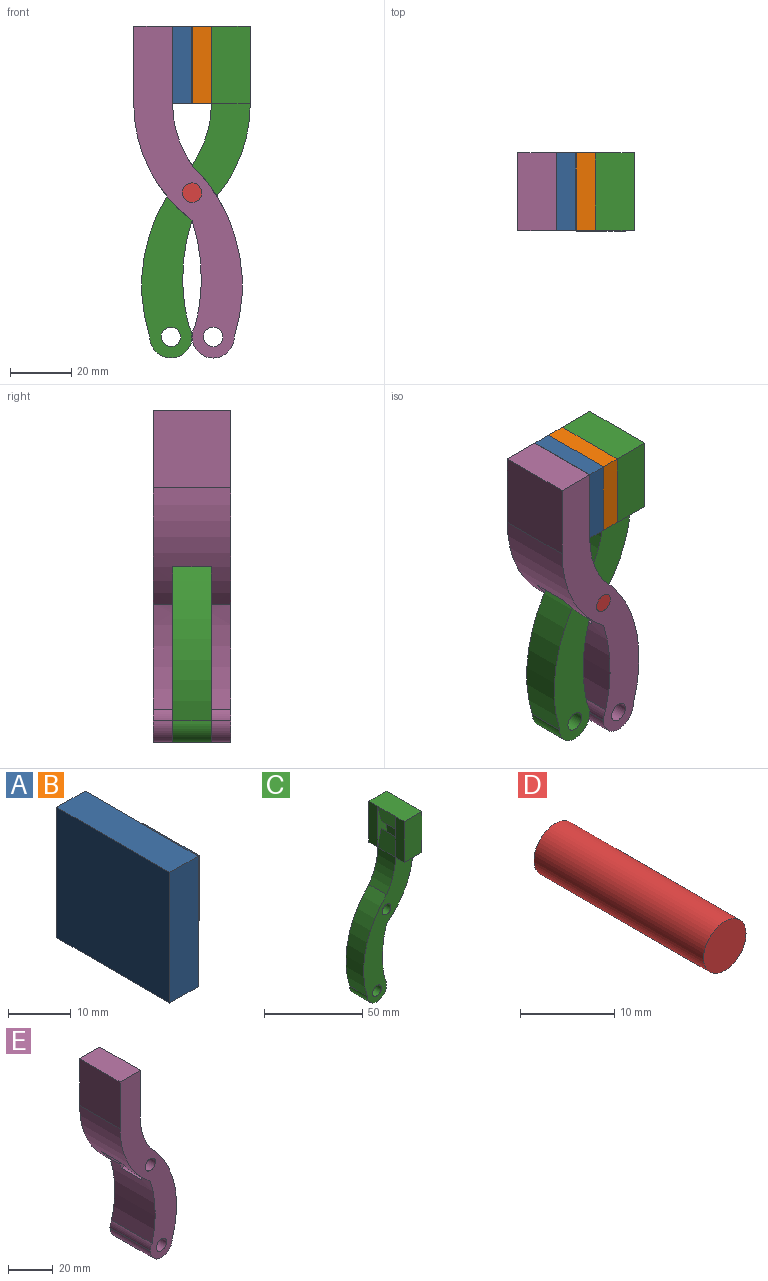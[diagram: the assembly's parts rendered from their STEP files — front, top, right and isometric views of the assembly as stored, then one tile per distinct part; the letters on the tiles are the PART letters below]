
ASSEMBLY  parts=5 mates=8
PART A: 14 faces, bbox 12.9x25.4x25.4 mm
  f0: plane 12.7x10.31mm, normal (0.97,0,-0.23), area 134.7mm2, adj f1,f5,f6,f8
  f1: plane 12.7x4.11mm, normal (-0.69,0,-0.72), area 72.5mm2, adj f0,f2,f5,f6
  f2: plane 12.7x12.7mm, normal (1,0,0), area 161.3mm2, adj f1,f3,f5,f6
  f3: plane 12.7x4.11mm, normal (-0.69,0,0.72), area 72.5mm2, adj f2,f4,f5,f6
  f4: plane 12.7x10.31mm, normal (0.97,0,0.23), area 134.7mm2, adj f3,f5,f6,f10
  f5: plane 25.4x6.59mm, normal (0,-1,0), area 73.3mm2, adj f0,f1,f2,f3,f4,f7
  f6: plane 25.4x6.59mm, normal (0,1,0), area 73.3mm2, adj f0,f1,f2,f3,f4,f9
  f7: plane 25.4x6.35mm, normal (1,0,0), area 161.3mm2, adj f5,f8,f10,f12
  f8: plane 25.4x6.35mm, normal (0,0,-1), area 161.3mm2, adj f0,f7,f9,f11,f12,f13
  f9: plane 25.4x6.35mm, normal (1,0,0), area 161.3mm2, adj f6,f8,f10,f13
  f10: plane 25.4x6.35mm, normal (0,0,1), area 161.3mm2, adj f4,f7,f9,f11,f12,f13
  f11: plane 25.4x25.4mm, normal (-1,0,0), area 645.2mm2, adj f8,f10,f12,f13
  f12: plane 25.4x6.35mm, normal (0,-1,0), area 161.3mm2, adj f7,f8,f10,f11
  f13: plane 25.4x6.35mm, normal (0,1,0), area 161.3mm2, adj f8,f9,f10,f11
PART B: same geometry as A
PART C: 24 faces, bbox 35.5x25.4x108.5 mm
  f0: plane 12.7x6.35mm, normal (0,0,-1), area 80.6mm2, adj f1,f5,f7,f22
  f1: plane 25.4x6.35mm, normal (-1,0,0), area 161.3mm2, adj f0,f2,f7,f13
  f2: plane 25.4x12.7mm, normal (0,0,1), area 322.6mm2, adj f1,f3,f5,f6,f7,f12
  f3: plane 25.4x6.35mm, normal (-1,0,0), area 161.3mm2, adj f2,f4,f6,f14
  f4: plane 12.7x6.35mm, normal (0,0,-1), area 80.6mm2, adj f3,f5,f6,f23
  f5: plane 25.4x25.4mm, normal (1,0,0), area 645.2mm2, adj f0,f2,f4,f6,f7,f20
  f6: plane 25.4x12.7mm, normal (0,1,0), area 322.6mm2, adj f2,f3,f4,f5
  f7: plane 25.4x12.7mm, normal (0,-1,0), area 322.6mm2, adj f0,f1,f2,f5
  f8: plane 12.7x10.31mm, normal (-0.97,0,0.23), area 134.7mm2, adj f9,f13,f14,f15
  f9: plane 12.7x4.11mm, normal (0.69,0,0.72), area 72.5mm2, adj f8,f10,f13,f14
  f10: plane 12.7x12.7mm, normal (-1,0,0), area 161.3mm2, adj f9,f11,f13,f14
  f11: plane 12.7x4.11mm, normal (0.69,0,-0.72), area 72.5mm2, adj f10,f12,f13,f14
  f12: plane 12.7x10.31mm, normal (-0.97,0,-0.23), area 134.7mm2, adj f2,f11,f13,f14
  f13: plane 25.4x6.59mm, normal (0,1,0), area 73.3mm2, adj f1,f8,f9,f10,f11,f12
  f14: plane 25.4x6.59mm, normal (0,-1,0), area 73.3mm2, adj f3,f8,f9,f10,f11,f12
  f15: cylinder r=34.92mm len=20.08mm, axis (0,1,0), area 271.7mm2, adj f8,f16,f22,f23
  f16: cylinder r=55.15mm len=56.19mm, axis (0,1,0), area 773.6mm2, adj f15,f17,f22,f23
  f17: cylinder r=6.91mm len=13.82mm, axis (0,1,0), area 325.1mm2, adj f16,f18,f22,f23
  f18: cylinder r=60.77mm len=34.41mm, axis (0,1,0), area 443.3mm2, adj f17,f20,f22,f23
  f19: cylinder r=3.17mm len=12.7mm, axis (0,1,0), area 253.4mm2, adj f22,f23
  f20: cylinder r=47.62mm len=38.1mm, axis (0,1,0), area 560.9mm2, adj f5,f18,f22,f23
  f21: cylinder r=3.17mm len=12.7mm, axis (0,1,0), area 253.4mm2, adj f22,f23
  f22: plane 83.14x35.52mm, normal (0,-1,0), area 1063.8mm2, adj f0,f15,f16,f17,f18,f19,f20,f21
  f23: plane 83.14x35.52mm, normal (0,1,0), area 1063.8mm2, adj f4,f15,f16,f17,f18,f19,f20,f21
PART D: 3 faces, bbox 6.4x25.4x6.4 mm
  f0: cylinder r=3.17mm len=25.4mm, axis (0,1,0), area 506.7mm2, adj f1,f2
  f1: plane 6.35x6.35mm, normal (0,-1,0), area 31.7mm2, adj f0
  f2: plane 6.35x6.35mm, normal (0,1,0), area 31.7mm2, adj f0
PART E: 27 faces, bbox 35.5x25.4x108.5 mm
  f0: cylinder r=3.17mm len=6.35mm, axis (0,1,0), area 126.7mm2, adj f9,f26
  f1: cylinder r=47.62mm len=38.1mm, axis (0,1,0), area 906.9mm2, adj f2,f8,f9,f10,f23,f25,f26
  f2: cylinder r=60.77mm len=34.41mm, axis (0,1,0), area 848.3mm2, adj f1,f9,f10,f18,f24,f25,f26
  f3: cylinder r=55.15mm len=56.19mm, axis (0,1,0), area 1318mm2, adj f4,f9,f10,f20,f24,f25,f26
  f4: cylinder r=34.92mm len=25.4mm, axis (0,1,0), area 501.4mm2, adj f3,f5,f6,f9,f10,f12,f23,f25
  f5: plane 25.4x6.35mm, normal (1,0,0), area 161.3mm2, adj f4,f7,f10,f16
  f6: plane 25.4x6.35mm, normal (1,0,0), area 161.3mm2, adj f4,f7,f9,f17
  f7: plane 25.4x12.7mm, normal (0,0,1), area 322.6mm2, adj f5,f6,f8,f9,f10,f13
  f8: plane 25.4x25.4mm, normal (-1,0,0), area 645.2mm2, adj f1,f7,f9,f10
  f9: plane 108.54x35.52mm, normal (0,1,0), area 1386.4mm2, adj f0,f1,f2,f3,f4,f6,f7,f8
  f10: plane 108.54x35.52mm, normal (0,-1,0), area 1386.4mm2, adj f1,f2,f3,f4,f5,f7,f8,f18
  f11: plane 12.7x4.11mm, normal (-0.69,0,0.72), area 72.5mm2, adj f12,f15,f16,f17
  f12: plane 12.7x10.31mm, normal (0.97,0,0.23), area 134.7mm2, adj f4,f11,f16,f17
  f13: plane 12.7x10.31mm, normal (0.97,0,-0.23), area 134.7mm2, adj f7,f14,f16,f17
  f14: plane 12.7x4.11mm, normal (-0.69,0,-0.72), area 72.5mm2, adj f13,f15,f16,f17
  f15: plane 12.7x12.7mm, normal (1,0,0), area 161.3mm2, adj f11,f14,f16,f17
  f16: plane 25.4x6.59mm, normal (0,1,0), area 73.3mm2, adj f5,f11,f12,f13,f14,f15
  f17: plane 25.4x6.59mm, normal (0,-1,0), area 73.3mm2, adj f6,f11,f12,f13,f14,f15
  f18: cylinder r=6.91mm len=25.4mm, axis (0,1,0), area 99mm2, adj f2,f9,f10,f19
  f19: cylinder r=6.91mm len=25.4mm, axis (0,1,0), area 1.8mm2, adj f9,f10,f18,f20
  f20: cylinder r=6.91mm len=25.4mm, axis (0,1,0), area 549.5mm2, adj f3,f9,f10,f19
  f21: cylinder r=3.17mm len=6.35mm, axis (0,1,0), area 126.7mm2, adj f10,f25
  f22: cylinder r=3.17mm len=25.4mm, axis (0,1,0), area 506.7mm2, adj f9,f10
  f23: cylinder r=11.93mm len=12.7mm, axis (0,1,0), area 173mm2, adj f1,f4,f25,f26
  f24: cylinder r=11.93mm len=12.7mm, axis (0,1,0), area 154.1mm2, adj f2,f3,f25,f26
  f25: plane 23.7x22.05mm, normal (0,1,0), area 250.4mm2, adj f1,f2,f3,f4,f21,f23,f24
  f26: plane 23.7x22.05mm, normal (0,-1,0), area 250.4mm2, adj f0,f1,f2,f3,f4,f23,f24
PLACE A rot(axis=(0,-0.71,0.71),180deg) t=(-63.61,6.42,-50.13)mm
PLACE B t=(-63.61,19.12,-37.43)mm
PLACE C t=(-63.61,19.12,-37.43)mm
PLACE D t=(-63.61,19.12,-37.43)mm
PLACE E t=(-63.61,19.12,-37.43)mm
MATE planar B.f2 <-> C.f10  axis (1,0,0) through (-50.67,19.12,-50.13)mm
MATE planar B.f5 <-> C.f13  axis (0,-1,0) through (-54.4,12.77,-50.13)mm
MATE pin_slot E.f0 <-> D.f0  axis (0,1,0) through (-63.61,31.82,-91.92)mm
MATE cylindrical D.f0 <-> C.f19  axis (0,1,0) through (-63.61,19.12,-91.92)mm
MATE cylindrical E.f0 <-> D.f0  axis (0,1,0) through (-63.61,31.82,-91.92)mm
MATE fastened A.f2 <-> E.f15  axis (-1,0,0) through (-76.54,19.12,-50.13)mm
MATE fastened B.f2 <-> C.f10  axis (1,0,0) through (-50.67,19.12,-50.13)mm
MATE pin_slot C.f19 <-> E.f0  axis (0,1,0) through (-63.61,25.47,-91.92)mm
